# Revit family: Storage-Freestanding-Teknion-JNFCP-Combo_Pedestal-R2015
name_source: partatom
category: Furniture
revit_build: Autodesk Revit Architecture 2016 (Build: 20150714_1515(x64)
units: mm (PartAtom-declared; Revit-internal decimal feet)

## family parameters
Always vertical = Yes
Cut with Voids When Loaded = No
OmniClass Number = 23.40.20.00
OmniClass Title = General Furniture and Specialties
Room Calculation Point = No
Shared = Yes
Work Plane-Based = No

## types (4) — shared parameters
Assembly Code = E2020200
Manufacturer = Teknion
Manufacturer Fax = 416.661.4586
Part Number = JNFCP
Product Documentation Link = https://www.teknion.com
Product Line = Cityline
Product Page URL = https://www.teknion.com
Series = Cityline
Sustainability Data = http://www.teknion.com
URL = www.teknion.com
Unit Weight URL = http://www.teknion.com
Warranty = http://www.teknion.com

## per-type parameters (varying)
| type | Description | Front Drawer Thickness | Front Finish | Model | Shelves Visibility |
| Solid, Open, Files | Combo Pedestal, Solid, Open, Files, 30" Width, 28" Height | 0.701 " | Source Laminate - Teknion - RV - Very White | JNFCPSO_3028_ | No |
| Solid, Shelves, Files | Combo Pedestal, Solid, Shelves, Files, 30" Width, 28" Height | 0.701 " | Source Laminate - Teknion - RV - Very White | JNFCPSS_3028_ | Yes |
| Metal, Open, Files | Combo Pedestal, Metal, Open, Files, 30" Width, 28" Height | 0.118 " | Mica - Teknion - V - Satin - Very White | JNFCPMO_3028_ | No |
| Metal, Shelves, Files | Combo Pedestal, Metal, Shelves, Files, 30" Width, 28" Height | 0.118 " | Mica - Teknion - V - Satin - Very White | JNFCPMS_3028_ | Yes |

## geometry (parser evidence)
native form markers: Sweep x2
no freeform markers — native parametric forms only
